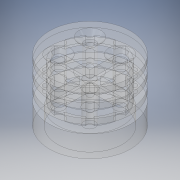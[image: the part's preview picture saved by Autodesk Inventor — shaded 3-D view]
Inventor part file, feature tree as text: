
AUTODESK INVENTOR PART (.ipt)
format: ipt  version: 2019 (Build 230136000, 136)  size: 317,952 bytes
history: native  units: mm
features: sketch x9, extrude x7, other x3, revolve x1, hole x1
ambient origin geometry x8: Origin, YZ Plane, XZ Plane, XY Plane, X Axis, Y Axis, Z Axis, Center Point
bodies: Body1 (feature_tree)
feature tree (21):
  other  "Bryła1"
  extrude  "Wyciągnięcie proste1"  Depth=20.0mm
  other  "Płaszczyzna konstrukcyjna1"
  revolve  "Obrót1"
  extrude  "Wyciągnięcie proste6"  Depth=25.0mm
  extrude  "Wyciągnięcie proste7"  Depth=5.0mm TaperAngle=0.0deg
  extrude  "Wyciągnięcie proste8"  Depth=2.5mm
  other  "Płaszczyzna konstrukcyjna2"
  extrude  "Wyciągnięcie proste9"  Depth=19.0mm
  extrude  "Wyciągnięcie proste10"  Depth=3.0mm
  hole  "Otwór1"  [1 undecoded]
  extrude  "Wyciągnięcie proste11"  TaperAngle=45.0deg  [1 undecoded]
  sketch  "Szkic1"
  sketch  "Szkic5"
  sketch  "Szkic7"
  sketch  "Szkic8"
  sketch  "Szkic9"
  sketch  "Szkic10"
  sketch  "Szkic11"
  sketch  "Szkic12"
  sketch  "Szkic13"
note: 2 required parameter values undecoded (feature->parameter linkage not recoverable at this tier; creation-order binding heuristic only, values carry confidence <= 0.55)
